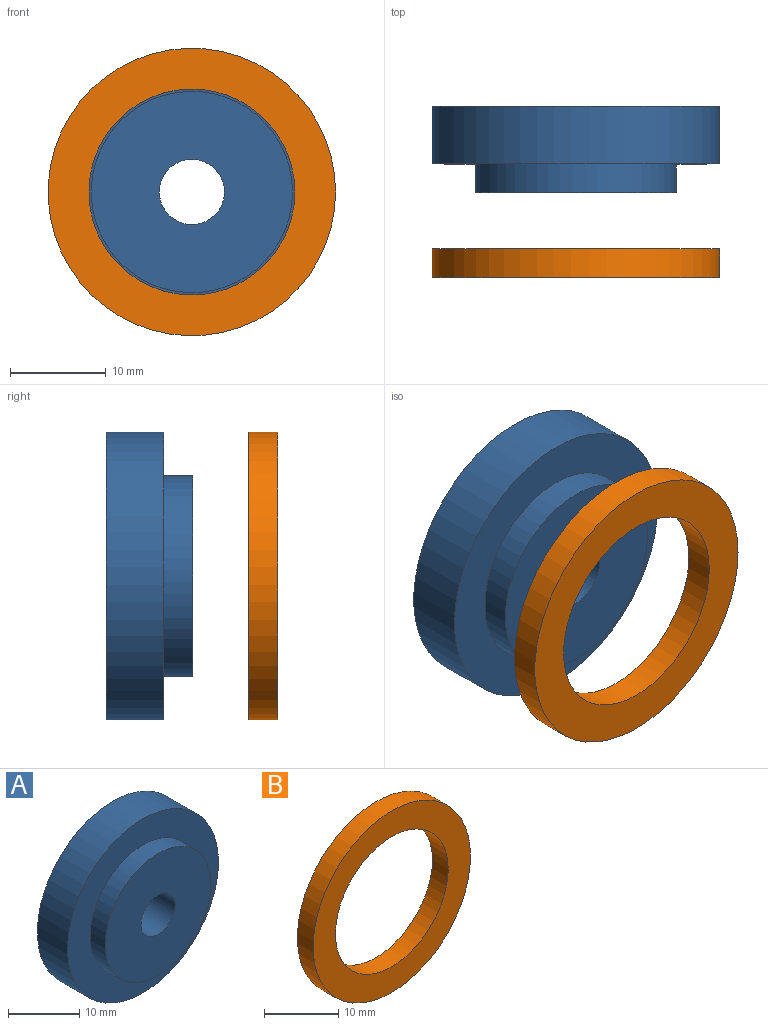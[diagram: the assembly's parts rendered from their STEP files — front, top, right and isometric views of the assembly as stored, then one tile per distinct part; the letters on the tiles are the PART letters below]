
ASSEMBLY  parts=2 mates=1
PART A: 6 faces, bbox 30x9x30 mm
  f0: cylinder r=15mm len=30mm, axis (0,1,0), area 565.5mm2, adj f1,f2
  f1: plane 30x30mm, normal (0,-1,0), area 360.5mm2, adj f0,f3
  f2: plane 30x30mm, normal (0,1,0), area 670.5mm2, adj f0,f5
  f3: cylinder r=10.5mm len=21mm, axis (0,1,0), area 197.9mm2, adj f1,f4
  f4: plane 21x21mm, normal (0,-1,0), area 310mm2, adj f3,f5
  f5: cylinder r=3.4mm len=9mm, axis (0,-1,0), area 192.3mm2, adj f2,f4
PART B: 4 faces, bbox 30x3x30 mm
  f0: cylinder r=10.75mm len=21.5mm, axis (0,1,0), area 202.6mm2, adj f2,f3
  f1: cylinder r=15mm len=30mm, axis (0,1,0), area 282.7mm2, adj f2,f3
  f2: plane 30x30mm, normal (0,-1,0), area 343.8mm2, adj f0,f1
  f3: plane 30x30mm, normal (0,1,0), area 343.8mm2, adj f0,f1
PLACE A t=(-10.97,13.22,-11.78)mm
PLACE B t=(-10.97,-1.65,-11.78)mm
MATE slider B.f0 <-> A.f0  axis (0,-1,0) through (-10.97,-4.65,-11.78)mm
